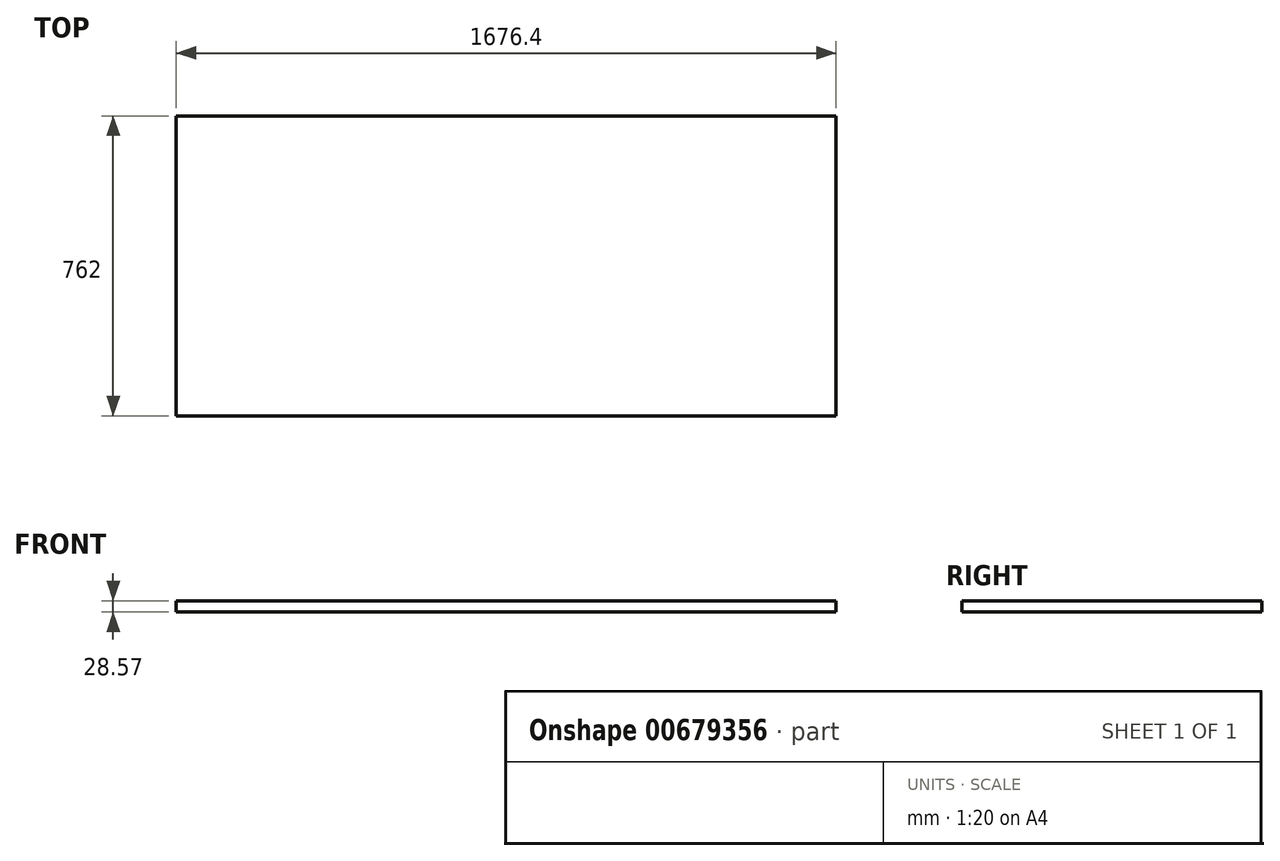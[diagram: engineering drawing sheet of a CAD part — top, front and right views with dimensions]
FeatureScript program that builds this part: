
annotation { "Feature Type Name" : "Feature", "Feature Type Description" : "" }
export const myFeature = defineFeature(function(context is Context, id is Id, definition is map)
    precondition{}
    {
        {
            var Q0;
            Q0=qCreatedBy(makeId("Top.planeOp"),FACE);
            var sketch = newSketch(context, id + "F0", { "sketchPlane" : qUnion([Q0])});
            skLineSegment(sketch, "E0.bottom", {"start": v(-838.2, 381) * mm, "end": v(838.2, 381) * mm});
            skLineSegment(sketch, "E0.top", {"start": v(-838.2, -381) * mm, "end": v(838.2, -381) * mm});
            skLineSegment(sketch, "E0.left", {"start": v(-838.2, 381) * mm, "end": v(-838.2, -381) * mm});
            skLineSegment(sketch, "E0.right", {"start": v(838.2, 381) * mm, "end": v(838.2, -381) * mm});
            skPoint(sketch, "E0.middle", {"position": v(0, 0) * mm});
            skSolve(sketch);
        }
        {
            var Q0;
            Q0=makeQuery(id+"F0.imprint","IMPRINT",FACE,{"disambiguationData":[TD([[makeQuery(id+"F0.imprint","IMPRINT",EDGE,{"derivedFrom":sQuery(id+"F0.wireOp",EDGE,"E0.bottom")}),-1.0]])]});
            extrude(context, id + "F1", {"entities" : qUnion([Q0]), "depth" : 28.57 * mm, "offsetDistance" : 25.4 * mm});
        }
    });
